# Revit family: result
name_source: partatom
category: Generic Models
revit_build: Autodesk Revit 2015 (Build: 20140903_1530(x64)
units: mm (PartAtom-declared; Revit-internal decimal feet)

## types (1)
- Default
    Brand url = http://www.gessi.it
    Design country = Italy
    Edition number = 1
    IFC Classification = Sanitary Terminal
    Installation instructions = https://www.gessi.com
    Manufacturer country = Italy
    Manufacturer name = Gessi
    Material main = Sintered stone
    Material secondary = Brass
    Product Guid = b6e428e8-4ce5-4551-b9b2-bb0c18c3d879
    Product SKU = 59508
    Product certification = https://www.gessi.com
    Product data url = https://bimobject.com
    Product family = RILIEVO
    Product group = RILIEVO ACCESSORI
    Product name = RILIEVO ACCESSORI - Wall-mounted tumbler holder black - 59508
    Product url = https://www.gessi.com
    QR code = http://bimobject.com
    Technical description = https://www.gessi.com

## geometry (parser evidence)
native form markers: Sweep x2
no freeform markers — native parametric forms only
